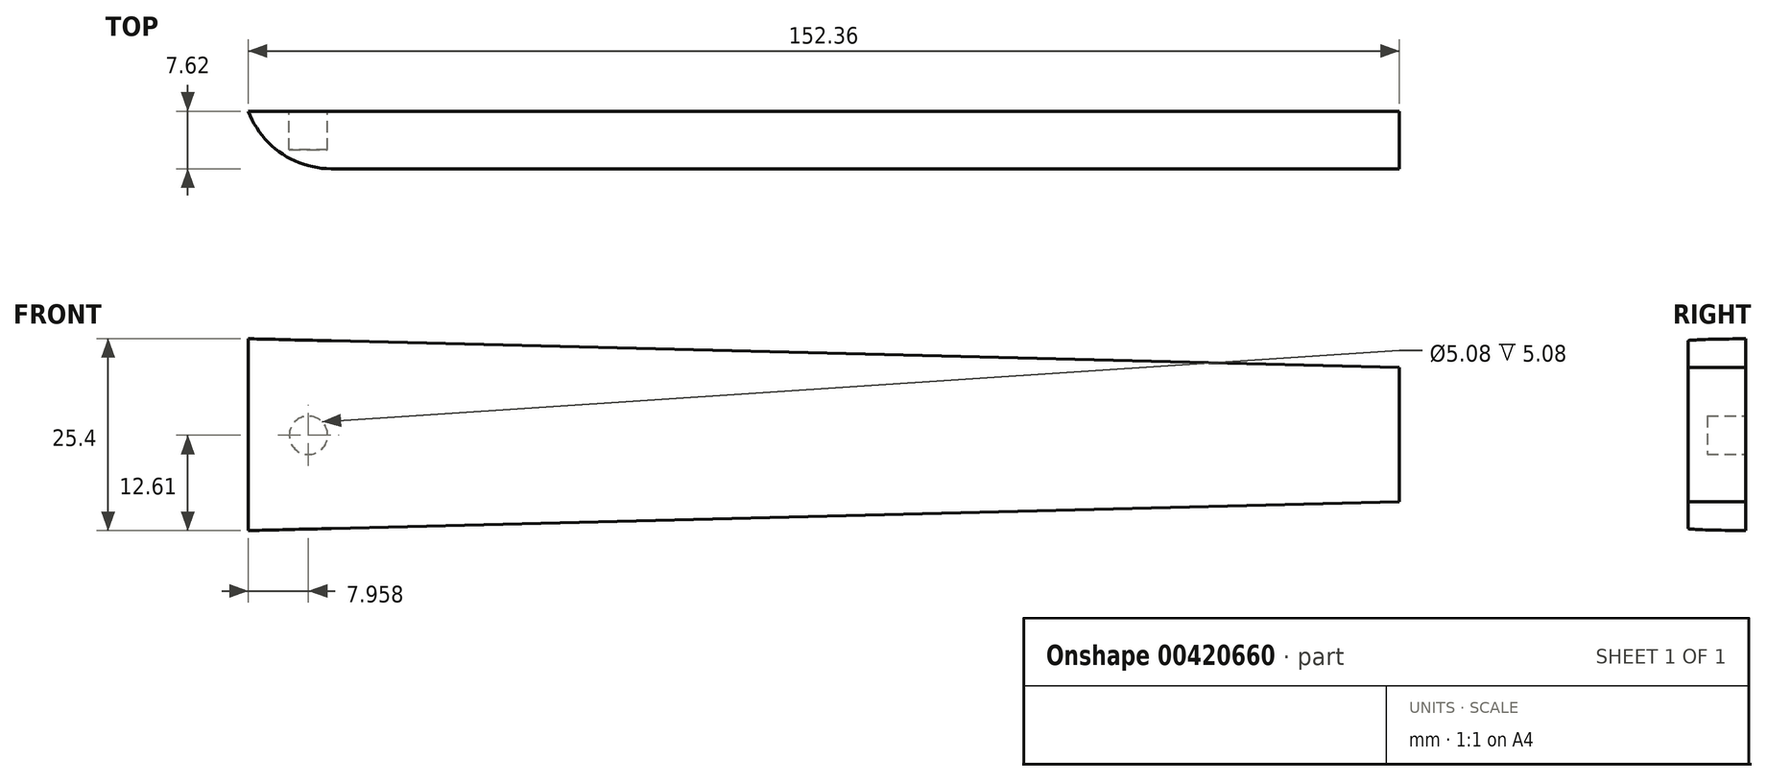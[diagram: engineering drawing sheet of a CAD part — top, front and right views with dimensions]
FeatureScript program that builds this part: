
annotation { "Feature Type Name" : "Feature", "Feature Type Description" : "" }
export const myFeature = defineFeature(function(context is Context, id is Id, definition is map)
    precondition{}
    {
        {
            var Q0;
            Q0=qCreatedBy(makeId("Front.planeOp"),FACE);
            var sketch = newSketch(context, id + "F0", { "sketchPlane" : qUnion([Q0])});
            skLineSegment(sketch, "E0", {"start": v(-48.84, -19.93) * mm, "end": v(103.52, -16.12) * mm});
            skLineSegment(sketch, "E1", {"start": v(-48.84, 5.47) * mm, "end": v(103.52, 1.66) * mm});
            skLineSegment(sketch, "E2", {"start": v(-48.84, 5.47) * mm, "end": v(-48.84, -19.93) * mm});
            skLineSegment(sketch, "E3", {"start": v(103.52, 1.66) * mm, "end": v(103.52, -16.12) * mm});
            skSolve(sketch);
        }
        {
            var Q0;
            Q0 = qSketchRegion(id + "F0", true);
            extrude(context, id + "F1", {"entities" : qUnion([Q0]), "depth" : 7.62 * mm});
        }
        {
            var Q0;
            Q0=makeQuery(id+"F1.opExtrude","CAP_EDGE",EDGE,{"disambiguationData":[OSD([sQuery(id+"F0.wireOp",EDGE,"E2")])],"isStart":false});
            fillet(context, id + "F2", {"entities" : qUnion([Q0]), "radius" : 11.68 * mm, "tangentPropagation" : true, "allowEdgeOverflow" : false});
        }
        {
            var Q0;
            Q0=makeQuery(id+"F1.opExtrude","CAP_FACE",FACE,{"disambiguationData":[OSD([sQuery(id+"F0.wireOp",EDGE,"E0"),sQuery(id+"F0.wireOp",EDGE,"E1"),sQuery(id+"F0.wireOp",EDGE,"E2"),sQuery(id+"F0.wireOp",EDGE,"E3")])],"isStart":true});
            var sketch = newSketch(context, id + "F3", { "sketchPlane" : qUnion([Q0])});
            skCircle(sketch, "E4", {"center": v(40.88, -7.32) * mm, "radius": 2.54 * mm});
            skSolve(sketch);
        }
        {
            var Q0;
            Q0 = qSketchRegion(id + "F3", true);
            extrude(context, id + "F4", {"entities" : qUnion([Q0]), "operationType" : NewBodyOperationType.REMOVE, "oppositeDirection" : true, "depth" : 5.08 * mm});
        }
    });
